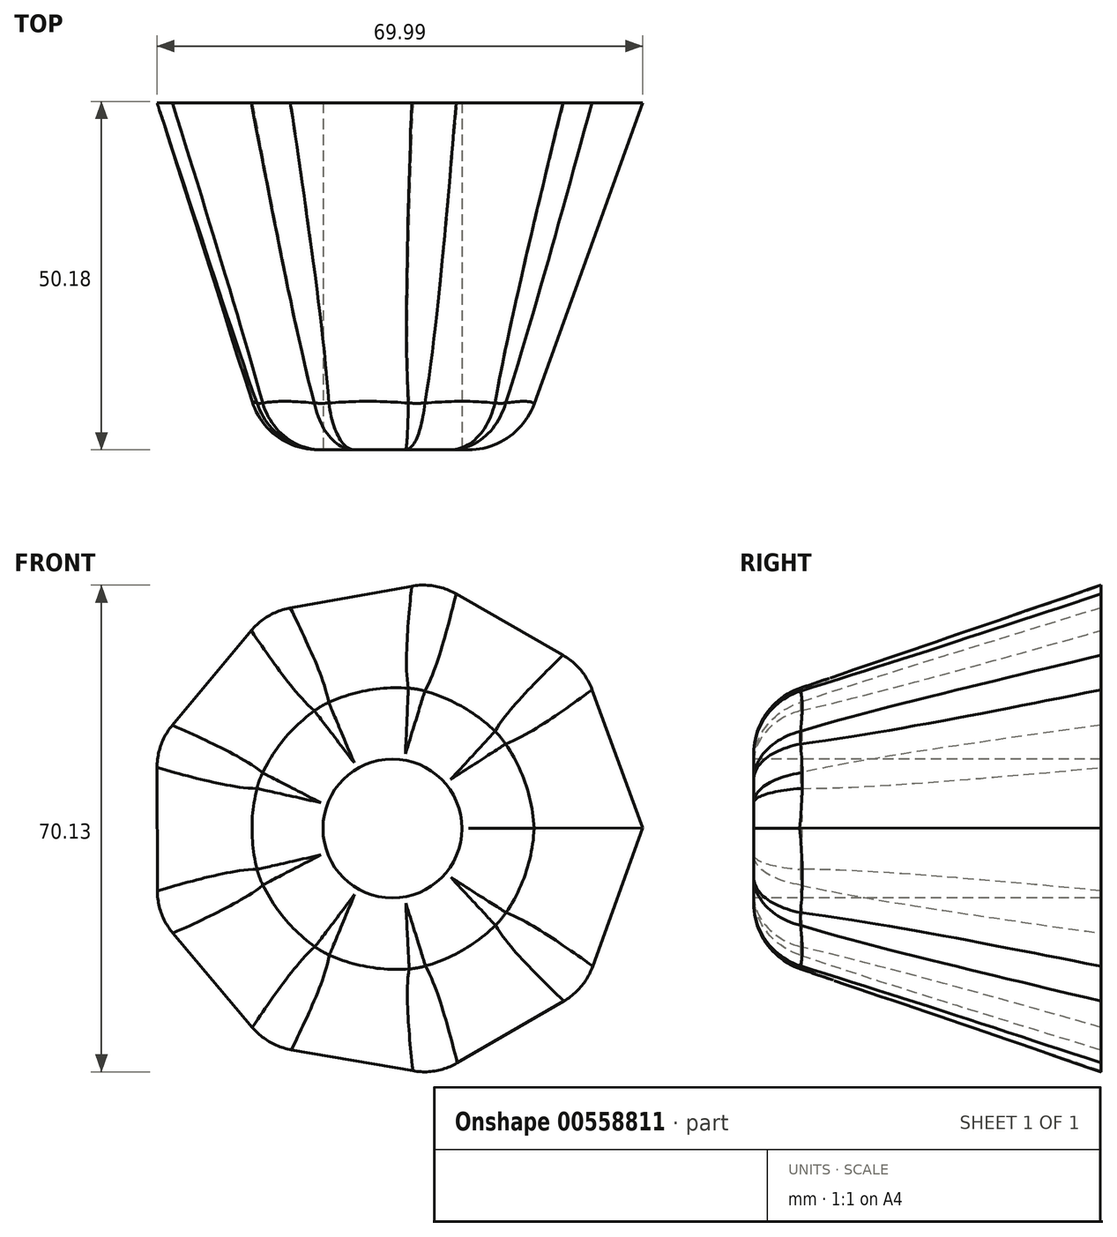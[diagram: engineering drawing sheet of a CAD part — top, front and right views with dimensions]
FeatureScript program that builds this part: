
annotation { "Feature Type Name" : "Feature", "Feature Type Description" : "" }
export const myFeature = defineFeature(function(context is Context, id is Id, definition is map)
    precondition{}
    {
        {
            var Q0;
            Q0=qCreatedBy(makeId("Front.planeOp"),FACE);
            var sketch = newSketch(context, id + "F0", { "sketchPlane" : qUnion([Q0])});
            skCircle(sketch, "E0.cCircle", {"center": v(0, 0) * mm, "radius": 33.9 * mm, "construction": true});
            skLineSegment(sketch, "E0.0", {"start": v(27.7, -23.11) * mm, "end": v(6.36, -35.5) * mm});
            skLineSegment(sketch, "E0.1", {"start": v(6.36, -35.5) * mm, "end": v(-17.95, -31.28) * mm});
            skLineSegment(sketch, "E0.2", {"start": v(-17.95, -31.28) * mm, "end": v(-33.86, -12.42) * mm});
            skLineSegment(sketch, "E0.3", {"start": v(-33.86, -12.42) * mm, "end": v(-33.93, 12.25) * mm});
            skLineSegment(sketch, "E0.4", {"start": v(-33.93, 12.25) * mm, "end": v(-18.12, 31.2) * mm});
            skLineSegment(sketch, "E0.5", {"start": v(-18.12, 31.2) * mm, "end": v(6.17, 35.54) * mm});
            skLineSegment(sketch, "E0.6", {"start": v(6.17, 35.54) * mm, "end": v(27.57, 23.26) * mm});
            skLineSegment(sketch, "E0.7", {"start": v(27.57, 23.26) * mm, "end": v(36.07, 0.1) * mm});
            skLineSegment(sketch, "E0.8", {"start": v(36.07, 0.1) * mm, "end": v(27.7, -23.11) * mm});
            skPoint(sketch, "E0.0.midPoint", {"position": v(17.02, -29.3) * mm});
            skSolve(sketch);
        }
        {
            var Q0;
            Q0=qCreatedBy(makeId("Front.planeOp"),FACE);
            var sketch = newSketch(context, id + "F1", { "sketchPlane" : qUnion([Q0])});
            skCircle(sketch, "E1", {"center": v(0, 0) * mm, "radius": 17.91 * mm});
            skSolve(sketch);
        }
        {
            var Q0;
            Q0 = qSketchRegion(id + "F1", true);
            extrude(context, id + "F2", {"entities" : qUnion([Q0]), "depth" : 50 * mm, "offsetDistance" : 25 * mm});
        }
        {
            var Q0;
            Q0=makeQuery(id+"F2.opExtrude","CAP_FACE",FACE,{"disambiguationData":[OSD([sQuery(id+"F1.wireOp",EDGE,"E1")])],"isStart":false});
            var sketch = newSketch(context, id + "F3", { "sketchPlane" : qUnion([Q0])});
            skCircle(sketch, "E2", {"center": v(0, 0) * mm, "radius": 18.02 * mm});
            skSolve(sketch);
        }
        {
            var Q1;
            Q1 = qSketchRegion(id + "F0", true);
            var Q2;
            Q2 = qSketchRegion(id + "F3", true);
            loft(context, id + "F4", {"operationType" : NewBodyOperationType.ADD, "sheetProfilesArray" : [{ "sheetProfileEntities" : qUnion([Q1]) }, { "sheetProfileEntities" : qUnion([Q2]) }]});
        }
        {
            var Q0;
            Q0=makeQuery(id+"F4.opLoft","SWEPT_EDGE",EDGE,{"disambiguationData":[OSD([sQuery(id+"F0.wireOp",EDGE,"E0.5"),sQuery(id+"F0.wireOp",EDGE,"E0.6"),sQuery(id+"F0.wireOp",EDGE,"E0.7"),sQuery(id+"F3.wireOp",EDGE,"E2")])]});
            var Q1;
            Q1=makeQuery(id+"F4.opLoft","SWEPT_EDGE",EDGE,{"disambiguationData":[OSD([sQuery(id+"F0.wireOp",EDGE,"E0.6"),sQuery(id+"F0.wireOp",EDGE,"E0.7"),sQuery(id+"F0.wireOp",EDGE,"E0.8"),sQuery(id+"F3.wireOp",EDGE,"E2")])]});
            var Q2;
            Q2=makeQuery(id+"F4.opLoft","SWEPT_EDGE",EDGE,{"disambiguationData":[OSD([sQuery(id+"F0.wireOp",EDGE,"E0.0"),sQuery(id+"F0.wireOp",EDGE,"E0.7"),sQuery(id+"F0.wireOp",EDGE,"E0.8"),sQuery(id+"F3.wireOp",EDGE,"E2")])]});
            var Q3;
            Q3=makeQuery(id+"F4.opLoft","SWEPT_EDGE",EDGE,{"disambiguationData":[OSD([sQuery(id+"F0.wireOp",EDGE,"E0.4"),sQuery(id+"F0.wireOp",EDGE,"E0.5"),sQuery(id+"F0.wireOp",EDGE,"E0.6"),sQuery(id+"F3.wireOp",EDGE,"E2")])]});
            var Q4;
            Q4=makeQuery(id+"F4.opLoft","SWEPT_EDGE",EDGE,{"disambiguationData":[OSD([sQuery(id+"F0.wireOp",EDGE,"E0.0"),sQuery(id+"F0.wireOp",EDGE,"E0.8")])]});
            var Q5;
            Q5=makeQuery(id+"F4.opLoft","SWEPT_EDGE",EDGE,{"disambiguationData":[OSD([sQuery(id+"F0.wireOp",EDGE,"E0.0"),sQuery(id+"F0.wireOp",EDGE,"E0.1"),sQuery(id+"F0.wireOp",EDGE,"E0.2"),sQuery(id+"F3.wireOp",EDGE,"E2")])]});
            var Q6;
            Q6=makeQuery(id+"F4.opLoft","SWEPT_EDGE",EDGE,{"disambiguationData":[OSD([sQuery(id+"F0.wireOp",EDGE,"E0.1"),sQuery(id+"F0.wireOp",EDGE,"E0.2"),sQuery(id+"F0.wireOp",EDGE,"E0.3"),sQuery(id+"F3.wireOp",EDGE,"E2")])]});
            var Q7;
            Q7=makeQuery(id+"F4.opLoft","SWEPT_EDGE",EDGE,{"disambiguationData":[OSD([sQuery(id+"F0.wireOp",EDGE,"E0.2"),sQuery(id+"F0.wireOp",EDGE,"E0.3"),sQuery(id+"F0.wireOp",EDGE,"E0.4"),sQuery(id+"F3.wireOp",EDGE,"E2")])]});
            var Q8;
            Q8=makeQuery(id+"F4.opLoft","SWEPT_EDGE",EDGE,{"disambiguationData":[OSD([sQuery(id+"F0.wireOp",EDGE,"E0.3"),sQuery(id+"F0.wireOp",EDGE,"E0.4"),sQuery(id+"F0.wireOp",EDGE,"E0.5"),sQuery(id+"F3.wireOp",EDGE,"E2")])]});
            var Q9;
            Q9=makeQuery(id+"F4.opLoft","MID_CAP_EDGE",EDGE,{"disambiguationData":[OSD([sQuery(id+"F0.wireOp",EDGE,"E0.3"),sQuery(id+"F0.wireOp",EDGE,"E0.4"),sQuery(id+"F0.wireOp",EDGE,"E0.5"),sQuery(id+"F3.wireOp",EDGE,"E2")])],"capPos":1.0});
            var Q10;
            Q10=makeQuery(id+"F4.opLoft","MID_CAP_EDGE",EDGE,{"disambiguationData":[OSD([sQuery(id+"F0.wireOp",EDGE,"E0.2"),sQuery(id+"F0.wireOp",EDGE,"E0.3"),sQuery(id+"F0.wireOp",EDGE,"E0.4"),sQuery(id+"F3.wireOp",EDGE,"E2")])],"capPos":1.0});
            var Q11;
            Q11=makeQuery(id+"F4.opLoft","MID_CAP_EDGE",EDGE,{"disambiguationData":[OSD([sQuery(id+"F0.wireOp",EDGE,"E0.1"),sQuery(id+"F0.wireOp",EDGE,"E0.2"),sQuery(id+"F0.wireOp",EDGE,"E0.3"),sQuery(id+"F3.wireOp",EDGE,"E2")])],"capPos":1.0});
            var Q12;
            Q12=makeQuery(id+"F4.opLoft","MID_CAP_EDGE",EDGE,{"disambiguationData":[OSD([sQuery(id+"F0.wireOp",EDGE,"E0.4"),sQuery(id+"F0.wireOp",EDGE,"E0.5"),sQuery(id+"F0.wireOp",EDGE,"E0.6"),sQuery(id+"F3.wireOp",EDGE,"E2")])],"capPos":1.0});
            var Q13;
            Q13=makeQuery(id+"F4.opLoft","MID_CAP_EDGE",EDGE,{"disambiguationData":[OSD([sQuery(id+"F0.wireOp",EDGE,"E0.0"),sQuery(id+"F0.wireOp",EDGE,"E0.1"),sQuery(id+"F0.wireOp",EDGE,"E0.2"),sQuery(id+"F0.wireOp",EDGE,"E0.8"),sQuery(id+"F3.wireOp",EDGE,"E2")])],"capPos":1.0});
            var Q14;
            Q14=makeQuery(id+"F4.opLoft","MID_CAP_EDGE",EDGE,{"disambiguationData":[OSD([sQuery(id+"F0.wireOp",EDGE,"E0.0"),sQuery(id+"F0.wireOp",EDGE,"E0.8"),sQuery(id+"F3.wireOp",EDGE,"E2")])],"capPos":1.0});
            var Q15;
            Q15=makeQuery(id+"F4.opLoft","MID_CAP_EDGE",EDGE,{"disambiguationData":[OSD([sQuery(id+"F0.wireOp",EDGE,"E0.0"),sQuery(id+"F0.wireOp",EDGE,"E0.7"),sQuery(id+"F0.wireOp",EDGE,"E0.8"),sQuery(id+"F3.wireOp",EDGE,"E2")])],"capPos":1.0});
            var Q16;
            Q16=makeQuery(id+"F4.opLoft","MID_CAP_EDGE",EDGE,{"disambiguationData":[OSD([sQuery(id+"F0.wireOp",EDGE,"E0.6"),sQuery(id+"F0.wireOp",EDGE,"E0.7"),sQuery(id+"F0.wireOp",EDGE,"E0.8"),sQuery(id+"F3.wireOp",EDGE,"E2")])],"capPos":1.0});
            var Q17;
            Q17=makeQuery(id+"F4.opLoft","MID_CAP_EDGE",EDGE,{"disambiguationData":[OSD([sQuery(id+"F0.wireOp",EDGE,"E0.5"),sQuery(id+"F0.wireOp",EDGE,"E0.6"),sQuery(id+"F0.wireOp",EDGE,"E0.7"),sQuery(id+"F3.wireOp",EDGE,"E2")])],"capPos":1.0});
            fillet(context, id + "F5", {"entities" : qUnion([Q0, Q1, Q2, Q3, Q4, Q5, Q6, Q7, Q8, Q9, Q10, Q11, Q12, Q13, Q14, Q15, Q16, Q17]), "radius" : 10 * mm, "tangentPropagation" : true, "allowEdgeOverflow" : false});
        }
        {
            var Q0;
            Q0=qCreatedBy(makeId("Front.planeOp"),FACE);
            var sketch = newSketch(context, id + "F6", { "sketchPlane" : qUnion([Q0])});
            skCircle(sketch, "E3", {"center": v(0, 0) * mm, "radius": 10.01 * mm});
            skSolve(sketch);
        }
        {
            var Q0;
            Q0 = qSketchRegion(id + "F6", true);
            extrude(context, id + "F7", {"entities" : qUnion([Q0]), "operationType" : NewBodyOperationType.REMOVE, "endBound" : BoundingType.SYMMETRIC, "oppositeDirection" : true, "depth" : 100 * mm, "offsetDistance" : 25 * mm});
        }
    });
